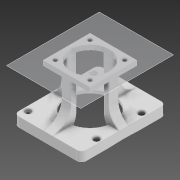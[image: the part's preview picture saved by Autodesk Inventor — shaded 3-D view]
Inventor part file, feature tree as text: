
AUTODESK INVENTOR PART (.ipt)
format: ipt  version: 2020 (Build 240168000, 168)  size: 335,360 bytes
history: native  units: in
note: dims shown in document units (in); Inventor stores cm internally (conversion verified against a paired STEP export)
features: extrude x7, sketch x6, fillet x5, plane x1, pattern_circular x1
ambient origin geometry x8: Origin, YZ Plane, XZ Plane, XY Plane, X Axis, Y Axis, Z Axis, Center Point
bodies: Solid1 (feature_tree)
feature tree (20):
  extrude  "Extrusion1"  Depth=2.4409in
  extrude  "Extrusion2"  Depth=1.8898in
  plane  "Work Plane1"
  extrude  "Extrusion3"  Depth=2.7559in
  extrude  "Extrusion4"  Depth=0.1969in
  fillet  "Fillet2"  Radius=0.3937in
  pattern_circular  "Circular Pattern1"  Count=9  [1 undecoded]
  fillet  "Fillet3"  Radius=0.1575in
  fillet  "Fillet4"  Radius=0.1575in
  extrude  "Extrusion5"  Depth=0.1575in
  sketch  "Sketch6"  dims[d10=3.1102in d11=3.5433in d12=0.1575in d13=0.1575in d14=0.1575in d15=0.1575in d16=0.3937in d17=0.0in d18=1.9685in d19=0.3937in d20=0.0in d21=1.7717in d22=1.4567in d23=1.4567in d24=0.1575in d25=0.1575in d26=0.1575in d27=0.1575in d28=1.9685in d29=1.9685in d30=0.1969in d31=0.0in d32=0.3543in d33=0.1969in d34=0.0in d36=0.7874in d37=1.5748in d38=360.0deg d40=0.7874in d41=0.7874in d42=0.2559in d43=0.2559in d44=0.2559in d45=0.2559in d46=0.1969in d47=0.0in d48=0.2362in d49=0.2362in d50=0.2362in d51=0.2362in d52=0.0787in d53=0.0in d54=0.2756in d55=0.0in d56=0.0394in d57=0.1969in]
  extrude  "Extrusion6"  Depth=0.1575in
  extrude  "Extrusion7"  Depth=0.3937in TaperAngle=0.0deg
  fillet  "Fillet5"  Radius=1.9685in
  fillet  "Fillet6"  Radius=0.3937in
  sketch  "Sketch1"  dims[d0=1.2205in d1=2.4409in]
  sketch  "Sketch2"  dims[d2=0.9449in d3=1.8898in]
  sketch  "Sketch3"  dims[d4=1.378in d5=2.7559in]
  sketch  "Sketch4"  dims[d6=0.1969in d7=0.1969in d8=0.3937in]
  sketch  "Sketch5"  dims[d9=2.8346in]
note: 1 required parameter value undecoded (feature->parameter linkage not recoverable at this tier; creation-order binding heuristic only, values carry confidence <= 0.55)
